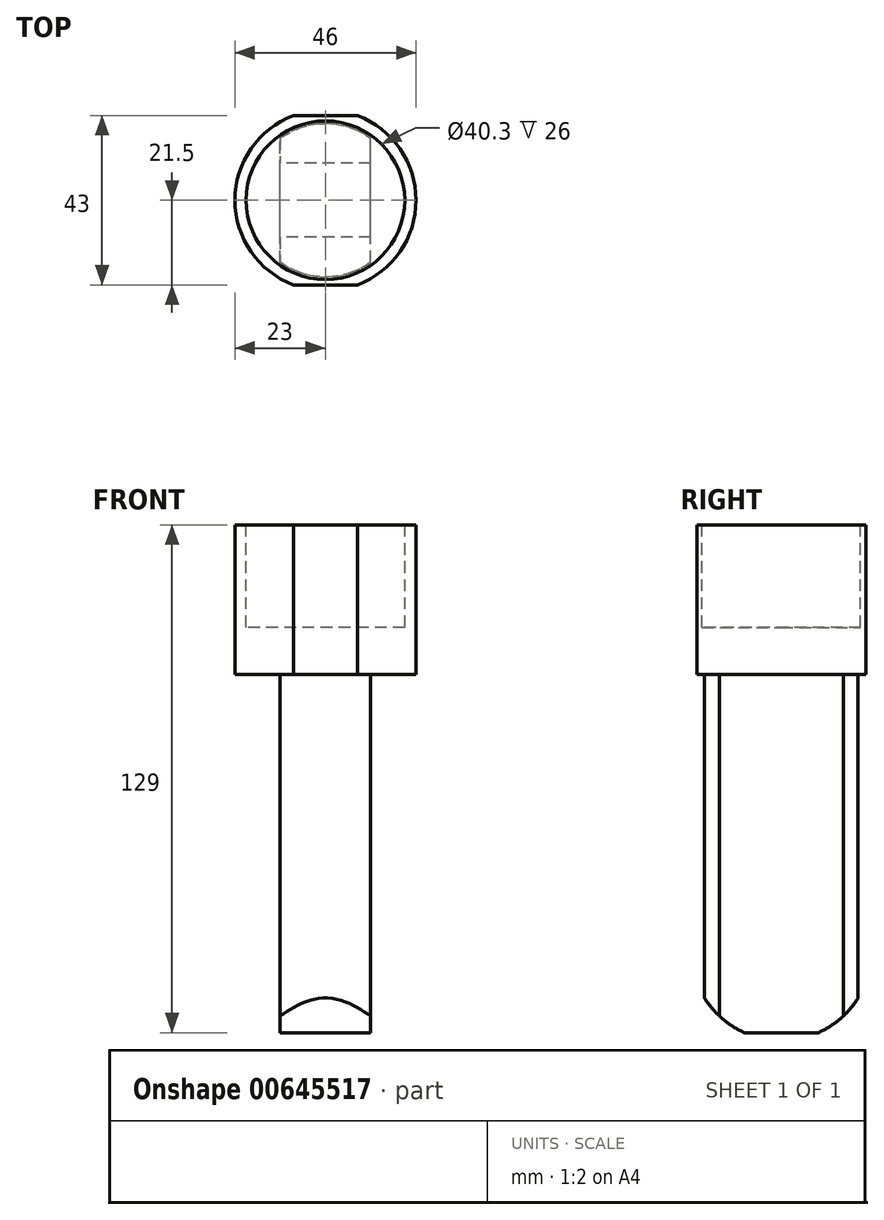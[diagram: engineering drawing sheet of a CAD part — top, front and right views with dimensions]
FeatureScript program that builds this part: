
annotation { "Feature Type Name" : "Feature", "Feature Type Description" : "" }
export const myFeature = defineFeature(function(context is Context, id is Id, definition is map)
    precondition{}
    {
        {
            var Q0;
            Q0=qCreatedBy(makeId("Top.planeOp"),FACE);
            var sketch = newSketch(context, id + "F0", { "sketchPlane" : qUnion([Q0])});
            skArc(sketch, "E0", {"start": v(-8.17, 21.5) * mm, "mid": v(-23, 0) * mm, "end": v(-8.17, -21.5) * mm});
            skLineSegment(sketch, "E1", {"start": v(8.17, 21.5) * mm, "end": v(-8.17, 21.5) * mm});
            skLineSegment(sketch, "E2.MirrorCS", {"start": v(8.17, -21.5) * mm, "end": v(-8.17, -21.5) * mm});
            skArc(sketch, "E3.trimOffspring", {"start": v(8.17, -21.5) * mm, "mid": v(23, 0) * mm, "end": v(8.17, 21.5) * mm});
            skSolve(sketch);
        }
        {
            var Q0;
            Q0=makeQuery(id+"F0.imprint","IMPRINT",FACE,{"disambiguationData":[TD([[makeQuery(id+"F0.imprint","IMPRINT",EDGE,{"derivedFrom":sQuery(id+"F0.wireOp",EDGE,"E0")}),1.0]])]});
            extrude(context, id + "F1", {"entities" : qUnion([Q0]), "depth" : 38 * mm, "offsetDistance" : 25 * mm});
        }
        {
            var Q0;
            Q0=makeQuery(id+"F1.opExtrude","CAP_FACE",FACE,{"disambiguationData":[OSD([sQuery(id+"F0.wireOp",EDGE,"E0"),sQuery(id+"F0.wireOp",EDGE,"E1"),sQuery(id+"F0.wireOp",EDGE,"E2.MirrorCS"),sQuery(id+"F0.wireOp",EDGE,"E3.trimOffspring")])],"isStart":false});
            var sketch = newSketch(context, id + "F2", { "sketchPlane" : qUnion([Q0])});
            skCircle(sketch, "E4", {"center": v(0, 0) * mm, "radius": 20.15 * mm});
            skSolve(sketch);
        }
        {
            var Q0;
            Q0=makeQuery(id+"F2.imprint","IMPRINT",FACE,{"disambiguationData":[TD([[makeQuery(id+"F2.imprint","IMPRINT",EDGE,{"derivedFrom":sQuery(id+"F2.wireOp",EDGE,"E4")}),1.0]])]});
            var Q1;
            Q1=sQuery(id+"F2.wireOp",EDGE,"E4");
            extrude(context, id + "F3", {"entities" : qUnion([Q0]), "operationType" : NewBodyOperationType.REMOVE, "surfaceEntities" : qUnion([Q1]), "oppositeDirection" : true, "depth" : 26 * mm, "offsetDistance" : 25 * mm});
        }
        {
            var Q0;
            Q0=makeQuery(id+"F1.opExtrude","CAP_FACE",FACE,{"disambiguationData":[OSD([sQuery(id+"F0.wireOp",EDGE,"E0"),sQuery(id+"F0.wireOp",EDGE,"E1"),sQuery(id+"F0.wireOp",EDGE,"E2.MirrorCS"),sQuery(id+"F0.wireOp",EDGE,"E3.trimOffspring")])],"isStart":true});
            var sketch = newSketch(context, id + "F4", { "sketchPlane" : qUnion([Q0])});
            skLineSegment(sketch, "E5.left", {"start": v(11.5, 15.75) * mm, "end": v(11.5, -15.75) * mm});
            skLineSegment(sketch, "E5.right", {"start": v(-11.5, 15.75) * mm, "end": v(-11.5, -15.75) * mm});
            skPoint(sketch, "E5.middle", {"position": v(0, 0) * mm});
            skArc(sketch, "E6", {"start": v(11.5, 15.75) * mm, "mid": v(0, 19.5) * mm, "end": v(-11.5, 15.75) * mm});
            skArc(sketch, "E7.trimOffspring", {"start": v(-11.5, -15.75) * mm, "mid": v(0, -19.5) * mm, "end": v(11.5, -15.75) * mm});
            skSolve(sketch);
        }
        {
            var Q0;
            Q0=makeQuery(id+"F4.imprint","IMPRINT",FACE,{"disambiguationData":[TD([[makeQuery(id+"F4.imprint","IMPRINT",EDGE,{"derivedFrom":sQuery(id+"F4.wireOp",EDGE,"E5.left")}),-1.0]])]});
            extrude(context, id + "F5", {"entities" : qUnion([Q0]), "operationType" : NewBodyOperationType.ADD, "depth" : 91 * mm, "offsetDistance" : 25 * mm});
        }
        {
            var Q0;
            Q0=makeQuery(id+"F5.opExtrude","SWEPT_FACE",FACE,{"disambiguationData":[OSD([sQuery(id+"F4.wireOp",EDGE,"E5.right")])]});
            var sketch = newSketch(context, id + "F6", { "sketchPlane" : qUnion([Q0])});
            skArc(sketch, "E8", {"start": v(-23, -70) * mm, "mid": v(0, -93) * mm, "end": v(23, -70) * mm});
            skLineSegment(sketch, "E9", {"start": v(23, -70) * mm, "end": v(26.64, -96.23) * mm});
            skLineSegment(sketch, "E10", {"start": v(26.64, -96.23) * mm, "end": v(-29.54, -96.23) * mm});
            skLineSegment(sketch, "E11", {"start": v(-29.54, -96.23) * mm, "end": v(-23, -70) * mm});
            skSolve(sketch);
        }
        {
            var Q0;
            {var subQ0=sQuery(id+"F6.wireOp",EDGE,"E8");var subQ1=sQuery(id+"F4.wireOp",EDGE,"E5.right");var subQ4=makeQuery(id+"F5.opExtrude","CAP_EDGE",EDGE,{"disambiguationData":[OSD([subQ1])],"isStart":false});var subQ5=makeQuery(id+"F6.imprint","INTERSECT",VERTEX,{"disambiguationData":[OD(0.0)],"derivedFrom":[subQ4,subQ0]});Q0=makeQuery(id+"F6.imprint","IMPRINT",FACE,{"disambiguationData":[TD([[makeQuery(id+"F6.imprint","IMPRINT",EDGE,{"disambiguationData":[TD([[subQ5,1.0]])],"derivedFrom":subQ0}),-1.0]])]});}
            var Q1;
            {var subQ0=sQuery(id+"F6.wireOp",EDGE,"E8");var subQ1=sQuery(id+"F4.wireOp",EDGE,"E5.right");var subQ4=makeQuery(id+"F5.opExtrude","CAP_EDGE",EDGE,{"disambiguationData":[OSD([subQ1])],"isStart":false});var subQ5=makeQuery(id+"F6.imprint","INTERSECT",VERTEX,{"disambiguationData":[OD(1.0)],"derivedFrom":[subQ4,subQ0]});Q1=makeQuery(id+"F6.imprint","IMPRINT",FACE,{"disambiguationData":[TD([[makeQuery(id+"F6.imprint","IMPRINT",EDGE,{"disambiguationData":[TD([[subQ5,-1.0]])],"derivedFrom":subQ0}),-1.0]])]});}
            var Q2;
            {var subQ0=sQuery(id+"F6.wireOp",EDGE,"E9");Q2=makeQuery(id+"F6.imprint","IMPRINT",FACE,{"disambiguationData":[TD([[makeQuery(id+"F6.imprint","IMPRINT",EDGE,{"derivedFrom":subQ0}),-1.0]])]});}
            extrude(context, id + "F7", {"entities" : qUnion([Q0, Q1, Q2]), "operationType" : NewBodyOperationType.REMOVE, "endBound" : BoundingType.THROUGH_ALL, "oppositeDirection" : true, "depth" : 25 * mm, "offsetDistance" : 25 * mm});
        }
    });
